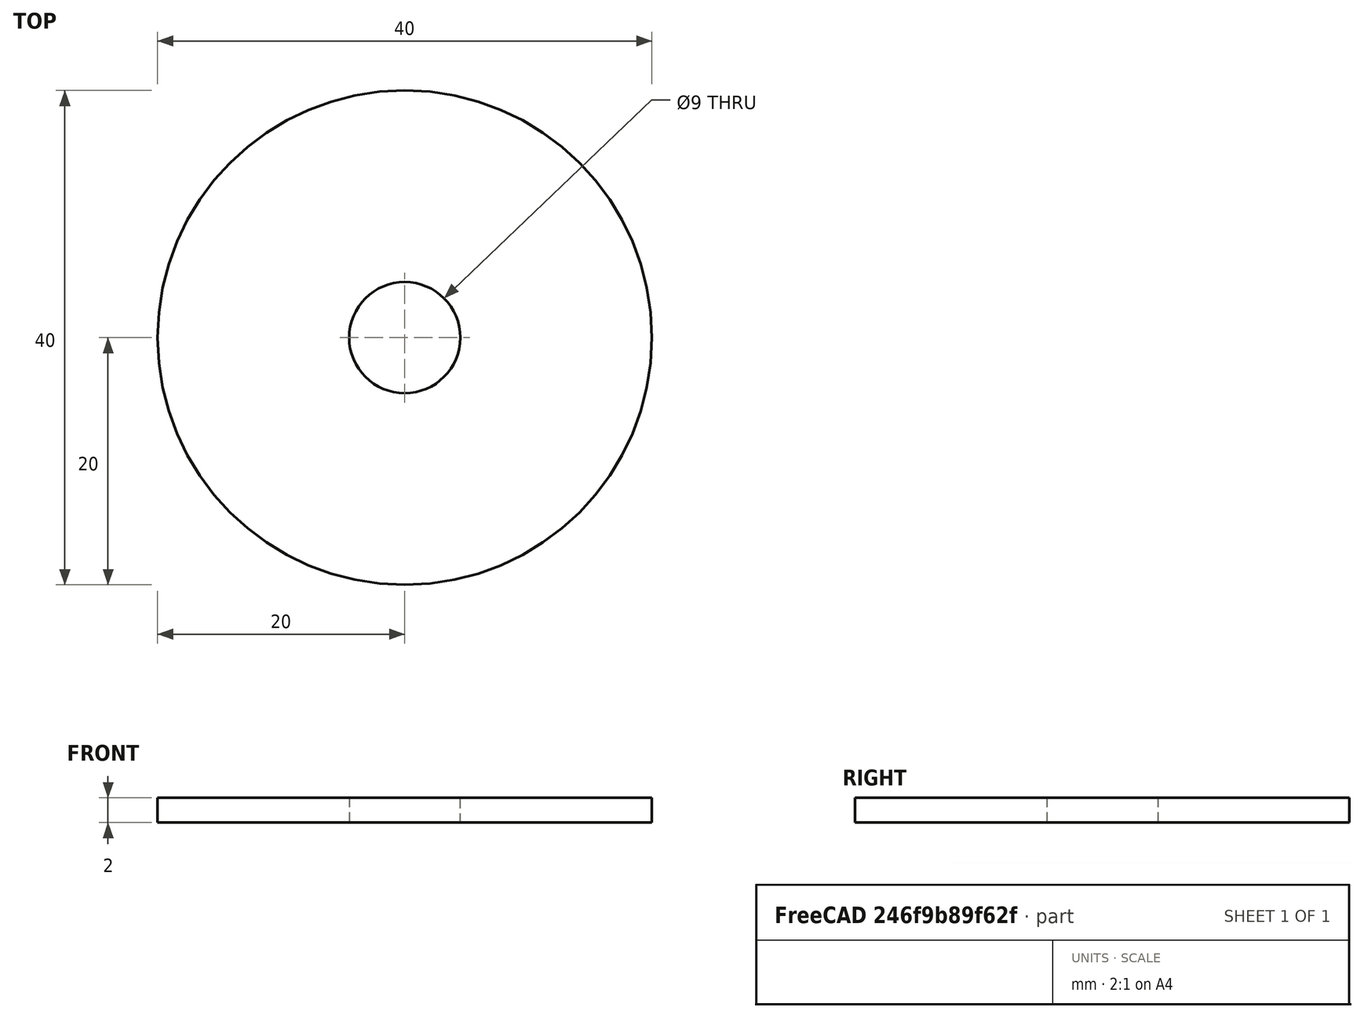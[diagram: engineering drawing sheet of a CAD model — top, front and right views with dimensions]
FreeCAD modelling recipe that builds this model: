
FCSTD DOCUMENT  (FreeCAD 0.19R24276 (Git))
Label: Shaiba_d9_d40_h_2
License: All rights reserved
LicenseURL: http://en.wikipedia.org/wiki/All_rights_reserved
objects: Sketcher::SketchObject×1, PartDesign::Pad×1, PartDesign::Body×1
note: 4 computed .brp shape members not serialized (recipe doc carries the construction recipe); baked Part::Feature solids carry a one-line shape summary decoded from their .brp

FEATURE [Sketcher::SketchObject] Sketch
  FullyConstrained = true
  MapMode = 5
  Support = -> [XY_Plane]
  sketch-geometry (2):
    g0: Circle CenterX=0 CenterY=0 CenterZ=0 NormalX=0 NormalY=0 NormalZ=1 AngleXU=0 Radius=4.5
    g1: Circle CenterX=0 CenterY=0 CenterZ=0 NormalX=0 NormalY=0 NormalZ=1 AngleXU=0 Radius=20
  constraints (4):
    c: Coincident(g0,g-1)
    c: Coincident(g1,g0)
    c: Diameter(g0) = 9
    c: Diameter(g1) = 40
FEATURE [PartDesign::Pad] Pad
  Direction = (1,1,1)
  Length = 2
  Length2 = 100
  Profile = -> Sketch
  Type = 0
FEATURE [PartDesign::Body] Body
  Group = -> [Sketch,Pad]
  Origin = -> Origin
  Tip = -> Pad
